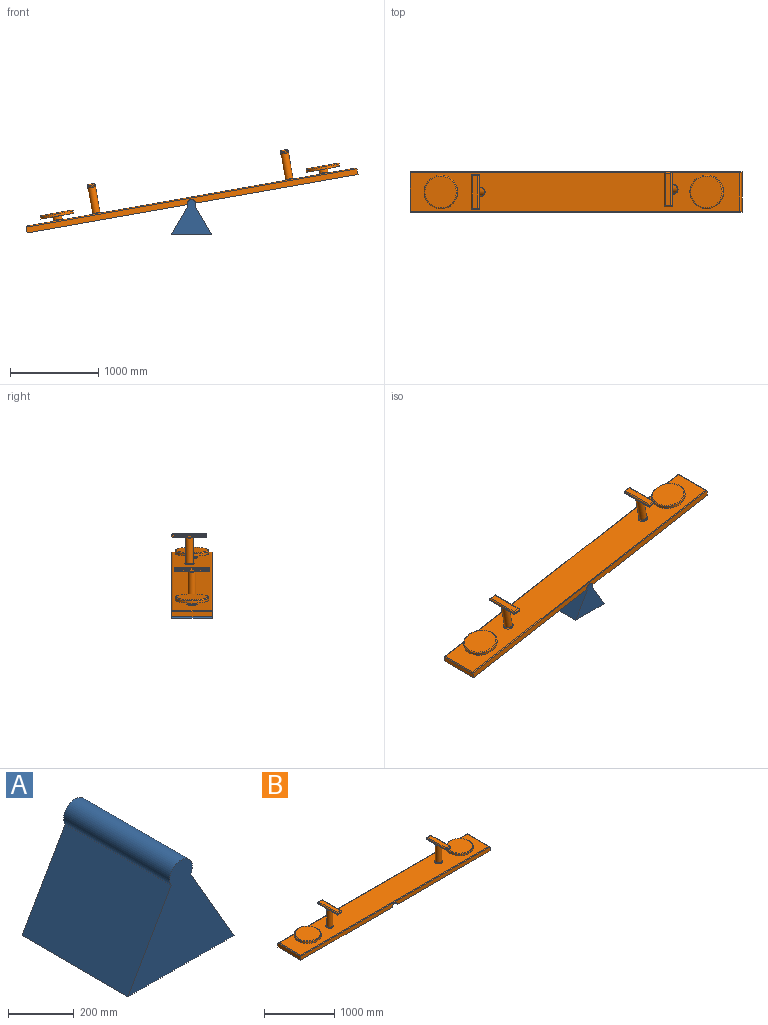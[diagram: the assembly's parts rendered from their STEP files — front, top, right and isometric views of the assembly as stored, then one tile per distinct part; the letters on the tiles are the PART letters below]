
ASSEMBLY  parts=2 mates=1
PART A: 6 faces, bbox 457.2x457.2x395.9 mm
  f0: plane 457.2x322.13mm, normal (0.87,0,0.5), area 170059.2mm2, adj f1,f3,f4,f5
  f1: cylinder r=49.21mm len=457.2mm, axis (0,-1,0), area 94251.3mm2, adj f0,f2,f4,f5
  f2: plane 457.2x322.13mm, normal (-0.87,0,0.5), area 170059.2mm2, adj f1,f3,f4,f5
  f3: plane 457.2x457.2mm, normal (0,0,-1), area 209031.8mm2, adj f0,f2,f4,f5
  f4: plane 457.2x395.95mm, normal (0,1,0), area 93488.6mm2, adj f0,f1,f2,f3
  f5: plane 457.2x395.95mm, normal (0,-1,0), area 93488.6mm2, adj f0,f1,f2,f3
PART B: 70 faces, bbox 3810x457.2x419.1 mm
  f0: plane 1867.79x457.2mm, normal (0,0,-1), area 853952.5mm2, adj f1,f2,f3,f15
  f1: plane 3810x66.04mm, normal (0,-1,0), area 247807.8mm2, adj f0,f2,f4,f6,f15,f66
  f2: plane 457.2x66.04mm, normal (1,0,0), area 30193.5mm2, adj f0,f1,f3,f67
  f3: plane 3810x66.04mm, normal (0,1,0), area 247807.8mm2, adj f0,f2,f4,f6,f15,f69
  f4: plane 457.2x66.04mm, normal (-1,0,0), area 30193.5mm2, adj f1,f3,f6,f68
  f5: plane 3789.68x436.88mm, normal (0,0,1), area 1613548.3mm2, adj f61,f62,f63,f65,f66,f67,f68,f69
  f6: plane 1843.78x457.2mm, normal (0,0,-1), area 842977.8mm2, adj f1,f3,f4,f15
  f7: cylinder r=50.8mm len=101.6mm, axis (0,0,-1), area 12971.7mm2, adj f10,f65
  f8: cylinder r=190.5mm len=381mm, axis (0,0,-1), area 33442.7mm2, adj f10,f64
  f9: plane 360.68x360.68mm, normal (0,0,1), area 102172.5mm2, adj f64
  f10: plane 381x381mm, normal (0,0,-1), area 105901.9mm2, adj f7,f8
  f11: cylinder r=50.8mm len=101.6mm, axis (0,0,-1), area 12971.7mm2, adj f14,f63
  f12: cylinder r=190.5mm len=381mm, axis (0,0,-1), area 33442.7mm2, adj f14,f60
  f13: plane 360.68x360.68mm, normal (0,0,1), area 102172.5mm2, adj f60
  f14: plane 381x381mm, normal (0,0,-1), area 105901.9mm2, adj f11,f12
  f15: cylinder r=49.21mm len=457.2mm, axis (0,-1,0), area 70688.5mm2, adj f0,f1,f3,f6
  f16: cylinder r=44.45mm len=294.64mm, axis (0,0,-1), area 82289.3mm2, adj f17,f18,f24,f28,f29,f32,f62
  f17: plane 153.04x63.5mm, normal (0,0,-1), area 9133.9mm2, adj f16,f25,f26,f27
  f18: plane 153.04x63.5mm, normal (0,0,-1), area 9133.9mm2, adj f16,f30,f31,f33
  f19: plane 88.9x12.7mm, normal (0,-1,0), area 1129mm2, adj f20,f22,f31,f35
  f20: plane 393.7x25.4mm, normal (1,0,0), area 5291.3mm2, adj f19,f21,f27,f28,f29,f30,f34
  f21: plane 88.9x12.7mm, normal (0,1,0), area 1129mm2, adj f20,f22,f26,f36
  f22: plane 393.7x25.4mm, normal (-1,0,0), area 5291.3mm2, adj f19,f21,f24,f25,f32,f33,f37
  f23: plane 368.3x63.5mm, normal (0,0,1), area 23387mm2, adj f34,f35,f36,f37
  f24: bspline ~32.55x13.48mm, area 299.3mm2, adj f16,f22,f25
  f25: cylinder r=12.7mm len=165.74mm, axis (0,-1,0), area 3214.3mm2, adj f17,f22,f24,f26
  f26: cylinder r=12.7mm len=88.9mm, axis (-1,0,0), area 1589.3mm2, adj f17,f21,f25,f27
  f27: cylinder r=12.7mm len=165.74mm, axis (0,1,0), area 3214.3mm2, adj f17,f20,f26,f28
  f28: bspline ~31.96x13.19mm, area 299.3mm2, adj f16,f20,f27
  f29: bspline ~31.96x13.19mm, area 299.3mm2, adj f16,f20,f30
  f30: cylinder r=12.7mm len=165.74mm, axis (0,1,0), area 3214.3mm2, adj f18,f20,f29,f31
  f31: cylinder r=12.7mm len=88.9mm, axis (1,0,0), area 1589.3mm2, adj f18,f19,f30,f33
  f32: bspline ~32.55x13.48mm, area 299.3mm2, adj f16,f22,f33
  f33: cylinder r=12.7mm len=165.74mm, axis (0,-1,0), area 3214.3mm2, adj f18,f22,f31,f32
  f34: cylinder r=12.7mm len=393.7mm, axis (0,-1,0), area 7669.8mm2, adj f20,f23,f35,f36
  f35: cylinder r=12.7mm len=88.9mm, axis (-1,0,0), area 1589.3mm2, adj f19,f23,f34,f37
  f36: cylinder r=12.7mm len=88.9mm, axis (1,0,0), area 1589.3mm2, adj f21,f23,f34,f37
  f37: cylinder r=12.7mm len=393.7mm, axis (0,1,0), area 7669.8mm2, adj f22,f23,f35,f36
  f38: cylinder r=44.45mm len=294.64mm, axis (0,0,-1), area 82289.3mm2, adj f39,f40,f46,f50,f51,f54,f61
  f39: plane 153.04x63.5mm, normal (0,0,-1), area 9133.9mm2, adj f38,f47,f48,f49
  f40: plane 153.04x63.5mm, normal (0,0,-1), area 9133.9mm2, adj f38,f52,f53,f55
  f41: plane 88.9x12.7mm, normal (0,-1,0), area 1129mm2, adj f42,f44,f53,f57
  f42: plane 393.7x25.4mm, normal (1,0,0), area 5291.3mm2, adj f41,f43,f49,f50,f51,f52,f56
  f43: plane 88.9x12.7mm, normal (0,1,0), area 1129mm2, adj f42,f44,f48,f58
  f44: plane 393.7x25.4mm, normal (-1,0,0), area 5291.3mm2, adj f41,f43,f46,f47,f54,f55,f59
  f45: plane 368.3x63.5mm, normal (0,0,1), area 23387.1mm2, adj f56,f57,f58,f59
  f46: bspline ~32.55x13.48mm, area 299.3mm2, adj f38,f44,f47
  f47: cylinder r=12.7mm len=165.74mm, axis (0,-1,0), area 3214.3mm2, adj f39,f44,f46,f48
  f48: cylinder r=12.7mm len=88.9mm, axis (-1,0,0), area 1589.3mm2, adj f39,f43,f47,f49
  f49: cylinder r=12.7mm len=165.74mm, axis (0,1,0), area 3214.3mm2, adj f39,f42,f48,f50
  f50: bspline ~31.96x13.19mm, area 299.3mm2, adj f38,f42,f49
  f51: bspline ~31.96x13.19mm, area 299.3mm2, adj f38,f42,f52
  f52: cylinder r=12.7mm len=165.74mm, axis (0,1,0), area 3214.3mm2, adj f40,f42,f51,f53
  f53: cylinder r=12.7mm len=88.9mm, axis (1,0,0), area 1589.3mm2, adj f40,f41,f52,f55
  f54: bspline ~32.55x13.48mm, area 299.3mm2, adj f38,f44,f55
  f55: cylinder r=12.7mm len=165.74mm, axis (0,-1,0), area 3214.3mm2, adj f40,f44,f53,f54
  f56: cylinder r=12.7mm len=393.7mm, axis (0,-1,0), area 7669.8mm2, adj f42,f45,f57,f58
  f57: cylinder r=12.7mm len=88.9mm, axis (-1,0,0), area 1589.3mm2, adj f41,f45,f56,f59
  f58: cylinder r=12.7mm len=88.9mm, axis (1,0,0), area 1589.3mm2, adj f43,f45,f56,f59
  f59: cylinder r=12.7mm len=393.7mm, axis (0,1,0), area 7669.8mm2, adj f44,f45,f57,f58
  f60: torus R=180.34mm, axis (0,0,1), area 18732.2mm2, adj f12,f13
  f61: torus R=54.61mm, axis (0,0,1), area 4827.4mm2, adj f5,f38
  f62: torus R=54.61mm, axis (0,0,1), area 4827.4mm2, adj f5,f16
  f63: torus R=60.96mm, axis (0,0,1), area 5464.2mm2, adj f5,f11
  f64: torus R=180.34mm, axis (0,0,1), area 18732.2mm2, adj f8,f9
  f65: torus R=60.96mm, axis (0,0,1), area 5464.2mm2, adj f5,f7
  f66: cylinder r=10.16mm len=3810mm, axis (-1,0,0), area 60687.1mm2, adj f1,f5,f67,f68
  f67: cylinder r=10.16mm len=457.2mm, axis (0,-1,0), area 7178.7mm2, adj f2,f5,f66,f69
  f68: cylinder r=10.16mm len=457.2mm, axis (0,1,0), area 7178.7mm2, adj f4,f5,f66,f69
  f69: cylinder r=10.16mm len=3810mm, axis (1,0,0), area 60687.1mm2, adj f3,f5,f67,f68
PLACE A t=(26.21,108.93,-115.6)mm fixed
PLACE B rot(axis=(0,-1,0),10deg) t=(94.97,108.93,-158.8)mm
MATE revolute B.f15 <-> A.f1  axis (0,-1,0) through (26.21,-119.67,231.13)mm
